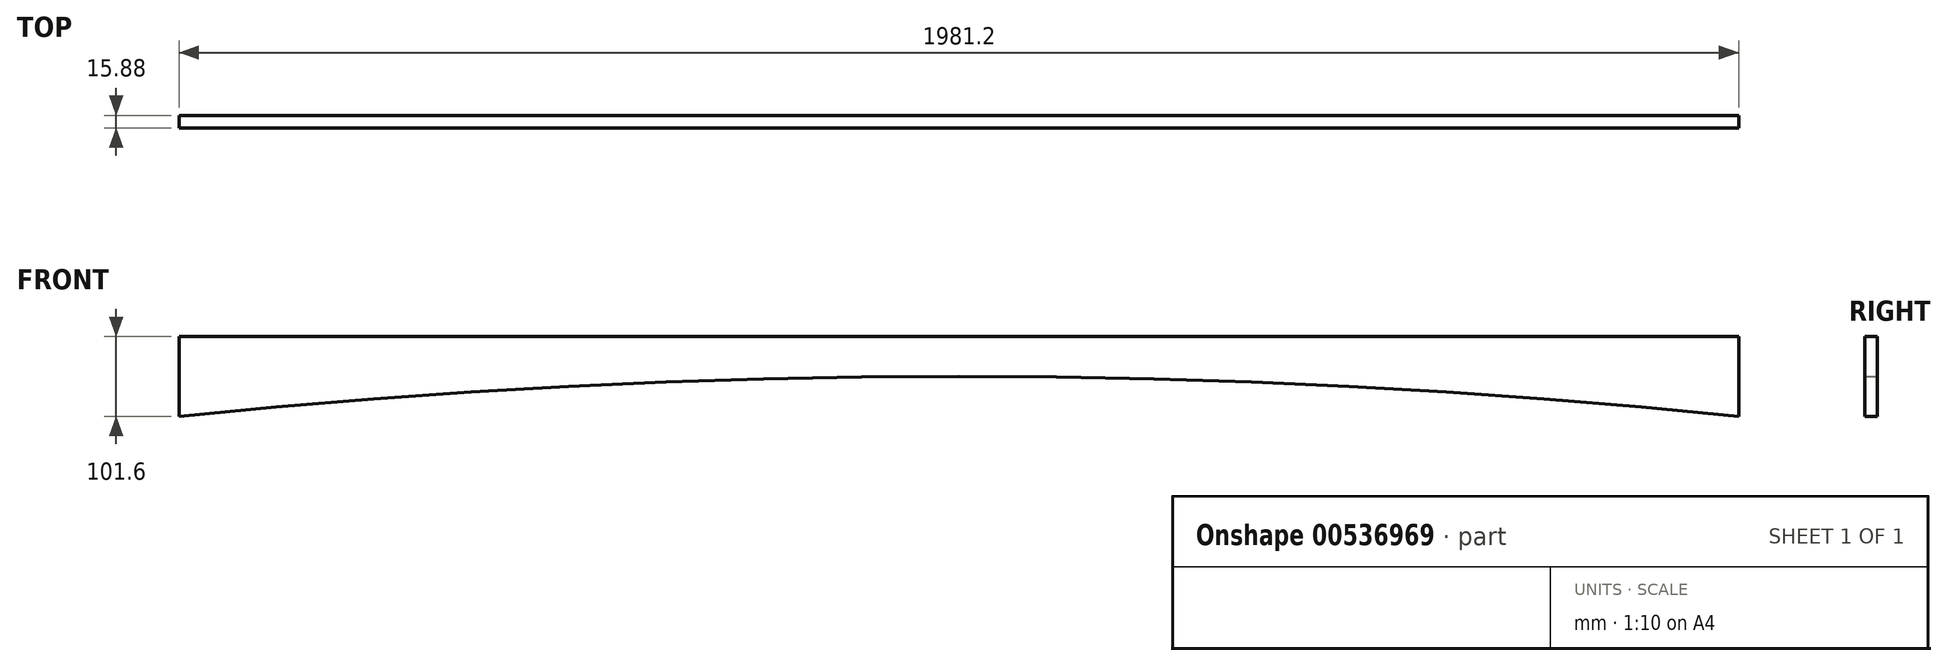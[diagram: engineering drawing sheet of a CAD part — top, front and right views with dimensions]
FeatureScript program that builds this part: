
annotation { "Feature Type Name" : "Feature", "Feature Type Description" : "" }
export const myFeature = defineFeature(function(context is Context, id is Id, definition is map)
    precondition{}
    {
        {
            var Q0;
            Q0=qCreatedBy(makeId("Front.planeOp"),FACE);
            var sketch = newSketch(context, id + "F0", { "sketchPlane" : qUnion([Q0])});
            skLineSegment(sketch, "E0", {"start": v(-120.66, 17.41) * mm, "end": v(1860.54, 17.41) * mm});
            skLineSegment(sketch, "E1", {"start": v(1860.54, 17.41) * mm, "end": v(1860.54, -58.79) * mm});
            skLineSegment(sketch, "E2", {"start": v(-120.66, 17.41) * mm, "end": v(-120.66, -58.79) * mm});
            skArc(sketch, "E3", {"start": v(1860.54, -58.79) * mm, "mid": v(869.94, -7.99) * mm, "end": v(-120.66, -58.79) * mm});
            skPoint(sketch, "E4.end.orphan", {"position": v(869.94, -7.99) * mm});
            skPoint(sketch, "E4.start.orphan", {"position": v(869.94, 17.41) * mm});
            skSolve(sketch);
        }
        {
            var Q0;
            Q0=makeQuery(id+"F0.imprint","IMPRINT",FACE,{"disambiguationData":[TD([[makeQuery(id+"F0.imprint","IMPRINT",EDGE,{"derivedFrom":sQuery(id+"F0.wireOp",EDGE,"E0")}),-1.0]])]});
            extrude(context, id + "F1", {"entities" : qUnion([Q0]), "depth" : 25.4 * mm, "offsetDistance" : 25.4 * mm});
        }
        {
            var Q0;
            Q0=makeQuery(id+"F1.opExtrude","SWEPT_BODY",BODY,{"disambiguationData":[OSD([sQuery(id+"F0.wireOp",EDGE,"E0"),sQuery(id+"F0.wireOp",EDGE,"E1"),sQuery(id+"F0.wireOp",EDGE,"E2"),sQuery(id+"F0.wireOp",EDGE,"E3")])]});
            deleteBodies(context, id + "F2", {"entities" : qUnion([Q0])});
        }
        {
            var Q0;
            Q0=qCreatedBy(makeId("Front.planeOp"),FACE);
            var sketch = newSketch(context, id + "F3", { "sketchPlane" : qUnion([Q0])});
            skLineSegment(sketch, "E5", {"start": v(-70.33, -377.06) * mm, "end": v(1910.87, -377.06) * mm});
            skLineSegment(sketch, "E6", {"start": v(1910.87, -377.06) * mm, "end": v(1910.87, -478.66) * mm});
            skLineSegment(sketch, "E7", {"start": v(-70.33, -377.06) * mm, "end": v(-70.33, -478.66) * mm});
            skArc(sketch, "E8", {"start": v(1910.87, -478.66) * mm, "mid": v(920.27, -427.86) * mm, "end": v(-70.33, -478.66) * mm});
            skPoint(sketch, "E9.end.orphan", {"position": v(920.27, -377.06) * mm});
            skSolve(sketch);
        }
        {
            var Q0;
            Q0 = qSketchRegion(id + "F3", true);
            extrude(context, id + "F4", {"entities" : qUnion([Q0]), "depth" : 15.88 * mm, "offsetDistance" : 25.4 * mm});
        }
    });
